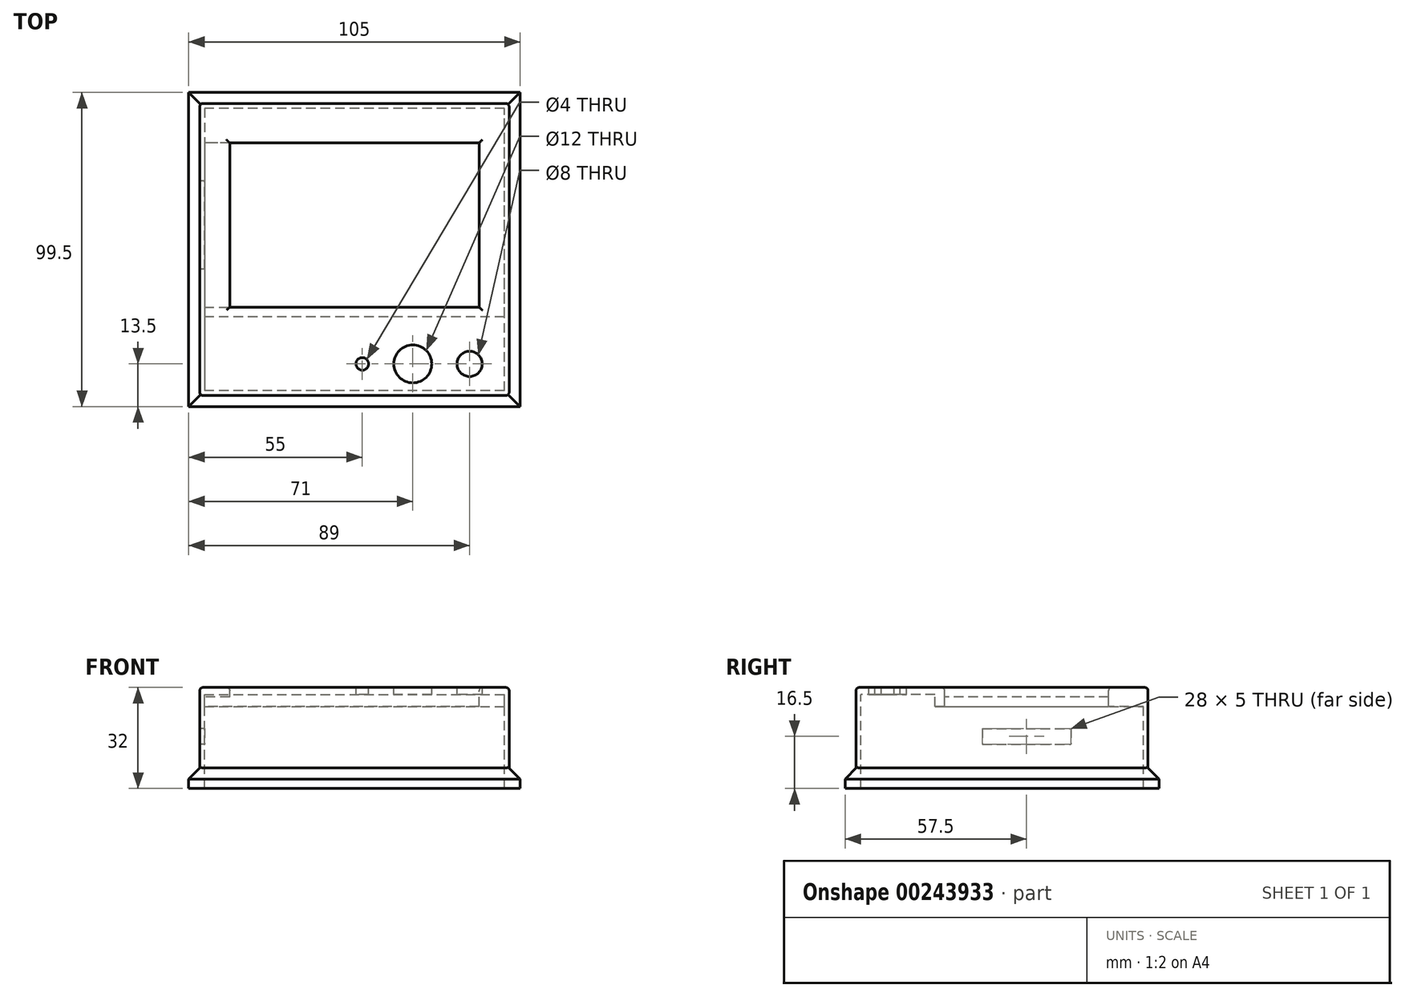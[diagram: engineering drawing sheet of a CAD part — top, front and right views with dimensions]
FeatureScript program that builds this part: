
annotation { "Feature Type Name" : "Feature", "Feature Type Description" : "" }
export const myFeature = defineFeature(function(context is Context, id is Id, definition is map)
    precondition{}
    {
        {
            var Q0;
            Q0=qCreatedBy(makeId("Top.planeOp"),FACE);
            var sketch = newSketch(context, id + "F0", { "sketchPlane" : qUnion([Q0])});
            skLineSegment(sketch, "E0", {"start": v(0, 0) * mm, "end": v(0, 52) * mm});
            skLineSegment(sketch, "E1", {"start": v(0, 52) * mm, "end": v(-87, 52) * mm});
            skLineSegment(sketch, "E2", {"start": v(-87, 0) * mm, "end": v(0, 0) * mm});
            skLineSegment(sketch, "E3.0", {"start": v(-87, 63) * mm, "end": v(-87, -26.5) * mm});
            skLineSegment(sketch, "E4.0", {"start": v(8, -26.5) * mm, "end": v(8, 63) * mm});
            skLineSegment(sketch, "E5.0", {"start": v(8, 63) * mm, "end": v(-87, 63) * mm});
            skLineSegment(sketch, "E6.0", {"start": v(-3, -5) * mm, "end": v(-3, -25) * mm, "construction": true});
            skLineSegment(sketch, "E7.0", {"start": v(-77, -18) * mm, "end": v(-3, -18) * mm, "construction": true});
            skLineSegment(sketch, "E8.0", {"start": v(-21, -5) * mm, "end": v(-21, -18) * mm, "construction": true});
            skLineSegment(sketch, "E9.0", {"start": v(-37, -5) * mm, "end": v(-37, -18) * mm, "construction": true});
            skCircle(sketch, "E10", {"center": v(-3, -18) * mm, "radius": 4 * mm});
            skCircle(sketch, "E11", {"center": v(-21, -18) * mm, "radius": 6 * mm});
            skCircle(sketch, "E12", {"center": v(-37, -18) * mm, "radius": 2 * mm});
            skPoint(sketch, "E13.orphan", {"position": v(-79, 0) * mm});
            skLineSegment(sketch, "E14.0", {"start": v(-88.5, 64.5) * mm, "end": v(-88.5, -28) * mm});
            skLineSegment(sketch, "E15.0", {"start": v(8, -26.5) * mm, "end": v(-87, -26.5) * mm});
            skLineSegment(sketch, "E16.0", {"start": v(9.5, -28) * mm, "end": v(9.5, 64.5) * mm});
            skLineSegment(sketch, "E17.0", {"start": v(9.5, 64.5) * mm, "end": v(-88.5, 64.5) * mm});
            skLineSegment(sketch, "E18.0", {"start": v(-79, 52) * mm, "end": v(-79, 0) * mm});
            skLineSegment(sketch, "E19.0", {"start": v(-77, -5) * mm, "end": v(-77, -18) * mm, "construction": true});
            skLineSegment(sketch, "E20.0", {"start": v(-77, -14) * mm, "end": v(-3, -14) * mm, "construction": true});
            skLineSegment(sketch, "E21.0", {"start": v(-87, -3) * mm, "end": v(8, -3) * mm});
            skLineSegment(sketch, "E22.0", {"start": v(9.5, -28) * mm, "end": v(-88.5, -28) * mm});
            skSolve(sketch);
        }
        {
            var Q0;
            {var subQ8=sQuery(id+"F0.wireOp",EDGE,"E0");Q0=makeQuery(id+"F0.imprint","IMPRINT",FACE,{"disambiguationData":[TD([[makeQuery(id+"F0.imprint","IMPRINT",EDGE,{"derivedFrom":subQ8}),-1.0]])]});}
            extrude(context, id + "F1", {"entities" : qUnion([Q0]), "oppositeDirection" : true, "depth" : 6 * mm});
        }
        {
            var Q0;
            {var subQ0=sQuery(id+"F0.wireOp",EDGE,"8c7ae999-3cc3-40bf-82e7-a0a417ca3e16.0");Q0=makeQuery(id+"F0.imprint","IMPRINT",FACE,{"disambiguationData":[TD([[makeQuery(id+"F0.imprint","IMPRINT",EDGE,{"derivedFrom":subQ0}),-1.0]])]});}
            var Q1;
            {var subQ3=sQuery(id+"F0.wireOp",EDGE,"E18.0");Q1=makeQuery(id+"F0.imprint","IMPRINT",FACE,{"disambiguationData":[TD([[makeQuery(id+"F0.imprint","IMPRINT",EDGE,{"derivedFrom":subQ3}),-1.0]])]});}
            extrude(context, id + "F2", {"entities" : qUnion([Q0, Q1]), "operationType" : NewBodyOperationType.ADD, "oppositeDirection" : true, "depth" : 3 * mm});
        }
        {
            var Q0;
            {var subQ1=sQuery(id+"F0.wireOp",EDGE,"E5.0");Q0=makeQuery(id+"F0.imprint","IMPRINT",FACE,{"disambiguationData":[TD([[makeQuery(id+"F0.imprint","IMPRINT",EDGE,{"derivedFrom":subQ1}),-1.0]])]});}
            extrude(context, id + "F3", {"entities" : qUnion([Q0]), "operationType" : NewBodyOperationType.ADD, "oppositeDirection" : true, "depth" : 32 * mm, "offsetDistance" : 25 * mm});
        }
        {
            var Q0;
            Q0=qCreatedBy(makeId("Right.planeOp"),FACE);
            cPlane(context, id + "F4", {"entities" : qUnion([Q0]), "cplaneType" : CPlaneType.OFFSET, "offset" : 88.5 * mm, "oppositeDirection" : true, "width" : 150 * mm, "height" : 150 * mm});
        }
        {
            var Q0;
            Q0=qCreatedBy(id+"F4.planeOp",FACE);
            var sketch = newSketch(context, id + "F5", { "sketchPlane" : qUnion([Q0])});
            skLineSegment(sketch, "E23.0", {"start": v(12, -13) * mm, "end": v(40, -13) * mm});
            skLineSegment(sketch, "E24.0", {"start": v(12, -18) * mm, "end": v(40, -18) * mm});
            skLineSegment(sketch, "E25.0", {"start": v(12, -13) * mm, "end": v(12, -18) * mm});
            skLineSegment(sketch, "E26.0", {"start": v(40, -13) * mm, "end": v(40, -18) * mm});
            skSolve(sketch);
        }
        {
            var Q0;
            Q0=makeQuery(id+"F5.imprint","IMPRINT",FACE,{"disambiguationData":[TD([[makeQuery(id+"F5.imprint","IMPRINT",EDGE,{"derivedFrom":sQuery(id+"F5.wireOp",EDGE,"E23.0")}),-1.0]])]});
            extrude(context, id + "F6", {"entities" : qUnion([Q0]), "operationType" : NewBodyOperationType.REMOVE, "depth" : 20 * mm});
        }
        {
            var Q0;
            Q0=makeQuery(id+"F0.imprint","IMPRINT",FACE,{"disambiguationData":[TD([[makeQuery(id+"F0.imprint","IMPRINT",EDGE,{"derivedFrom":sQuery(id+"F0.wireOp",EDGE,"E10")}),-1.0]])]});
            extrude(context, id + "F7", {"entities" : qUnion([Q0]), "operationType" : NewBodyOperationType.ADD, "oppositeDirection" : true, "depth" : 2.25 * mm});
        }
        {
            var Q0;
            Q0=qCreatedBy(makeId("Top.planeOp"),FACE);
            cPlane(context, id + "F8", {"entities" : qUnion([Q0]), "cplaneType" : CPlaneType.OFFSET, "offset" : 32 * mm, "oppositeDirection" : true, "width" : 150 * mm, "height" : 150 * mm});
        }
        {
            var Q0;
            Q0=qCreatedBy(id+"F8.planeOp",FACE);
            var sketch = newSketch(context, id + "F9", { "sketchPlane" : qUnion([Q0])});
            skLineSegment(sketch, "E27", {"start": v(0, 0) * mm, "end": v(8, 0) * mm, "construction": true});
            skLineSegment(sketch, "E28", {"start": v(8, 0) * mm, "end": v(8, -26.5) * mm, "construction": true});
            skLineSegment(sketch, "E29", {"start": v(8, -26.5) * mm, "end": v(-87, -26.5) * mm});
            skLineSegment(sketch, "E30", {"start": v(-87, -26.5) * mm, "end": v(-87, 63) * mm});
            skLineSegment(sketch, "E31", {"start": v(-87, 63) * mm, "end": v(8, 63) * mm});
            skLineSegment(sketch, "E32", {"start": v(8, 63) * mm, "end": v(8, -26.5) * mm});
            skLineSegment(sketch, "E33.0", {"start": v(13, 68) * mm, "end": v(13, -31.5) * mm});
            skLineSegment(sketch, "E34.0", {"start": v(13, -31.5) * mm, "end": v(-92, -31.5) * mm});
            skLineSegment(sketch, "E35.0", {"start": v(-92, -31.5) * mm, "end": v(-92, 68) * mm});
            skLineSegment(sketch, "E36.0", {"start": v(-92, 68) * mm, "end": v(13, 68) * mm});
            skSolve(sketch);
        }
        {
            var Q0;
            Q0=makeQuery(id+"F9.imprint","IMPRINT",FACE,{"disambiguationData":[TD([[makeQuery(id+"F9.imprint","IMPRINT",EDGE,{"derivedFrom":sQuery(id+"F9.wireOp",EDGE,"E29")}),1.0]])]});
            extrude(context, id + "F10", {"entities" : qUnion([Q0]), "operationType" : NewBodyOperationType.ADD, "depth" : 3 * mm, "offsetDistance" : 25 * mm});
        }
        {
            var Q0;
            Q0=makeQuery(id+"F10.boolean.opBoolean","INTERSECT",EDGE,{"derivedFrom":[makeQuery(id+"F3.opExtrude","SWEPT_FACE",FACE,{"disambiguationData":[OSD([sQuery(id+"F0.wireOp",EDGE,"E14.0")])]}),makeQuery(id+"F10.opExtrude","CAP_FACE",FACE,{"disambiguationData":[OSD([sQuery(id+"F9.wireOp",EDGE,"E29"),sQuery(id+"F9.wireOp",EDGE,"E30"),sQuery(id+"F9.wireOp",EDGE,"E31"),sQuery(id+"F9.wireOp",EDGE,"E32"),sQuery(id+"F9.wireOp",EDGE,"E33.0"),sQuery(id+"F9.wireOp",EDGE,"E34.0"),sQuery(id+"F9.wireOp",EDGE,"E35.0"),sQuery(id+"F9.wireOp",EDGE,"E36.0")])],"isStart":false})]});
            var Q1;
            Q1=makeQuery(id+"F10.boolean.opBoolean","INTERSECT",EDGE,{"derivedFrom":[makeQuery(id+"F3.opExtrude","SWEPT_FACE",FACE,{"disambiguationData":[OSD([sQuery(id+"F0.wireOp",EDGE,"E22.0")])]}),makeQuery(id+"F10.opExtrude","CAP_FACE",FACE,{"disambiguationData":[OSD([sQuery(id+"F9.wireOp",EDGE,"E29"),sQuery(id+"F9.wireOp",EDGE,"E30"),sQuery(id+"F9.wireOp",EDGE,"E31"),sQuery(id+"F9.wireOp",EDGE,"E32"),sQuery(id+"F9.wireOp",EDGE,"E33.0"),sQuery(id+"F9.wireOp",EDGE,"E34.0"),sQuery(id+"F9.wireOp",EDGE,"E35.0"),sQuery(id+"F9.wireOp",EDGE,"E36.0")])],"isStart":false})]});
            var Q2;
            Q2=makeQuery(id+"F10.boolean.opBoolean","INTERSECT",EDGE,{"derivedFrom":[makeQuery(id+"F3.opExtrude","SWEPT_FACE",FACE,{"disambiguationData":[OSD([sQuery(id+"F0.wireOp",EDGE,"E16.0")])]}),makeQuery(id+"F10.opExtrude","CAP_FACE",FACE,{"disambiguationData":[OSD([sQuery(id+"F9.wireOp",EDGE,"E29"),sQuery(id+"F9.wireOp",EDGE,"E30"),sQuery(id+"F9.wireOp",EDGE,"E31"),sQuery(id+"F9.wireOp",EDGE,"E32"),sQuery(id+"F9.wireOp",EDGE,"E33.0"),sQuery(id+"F9.wireOp",EDGE,"E34.0"),sQuery(id+"F9.wireOp",EDGE,"E35.0"),sQuery(id+"F9.wireOp",EDGE,"E36.0")])],"isStart":false})]});
            var Q3;
            Q3=makeQuery(id+"F10.boolean.opBoolean","INTERSECT",EDGE,{"derivedFrom":[makeQuery(id+"F3.opExtrude","SWEPT_FACE",FACE,{"disambiguationData":[OSD([sQuery(id+"F0.wireOp",EDGE,"E17.0")])]}),makeQuery(id+"F10.opExtrude","CAP_FACE",FACE,{"disambiguationData":[OSD([sQuery(id+"F9.wireOp",EDGE,"E29"),sQuery(id+"F9.wireOp",EDGE,"E30"),sQuery(id+"F9.wireOp",EDGE,"E31"),sQuery(id+"F9.wireOp",EDGE,"E32"),sQuery(id+"F9.wireOp",EDGE,"E33.0"),sQuery(id+"F9.wireOp",EDGE,"E34.0"),sQuery(id+"F9.wireOp",EDGE,"E35.0"),sQuery(id+"F9.wireOp",EDGE,"E36.0")])],"isStart":false})]});
            chamfer(context, id + "F11", {"entities" : qUnion([Q0, Q1, Q2, Q3]), "width" : 3.5 * mm, "tangentPropagation" : true});
        }
        {
            var Q0;
            Q0=makeQuery(id+"F3.opExtrude","SWEPT_EDGE",EDGE,{"disambiguationData":[OSD([sQuery(id+"F0.wireOp",EDGE,"E14.0"),sQuery(id+"F0.wireOp",EDGE,"E22.0")])]});
            var Q1;
            Q1=makeQuery(id+"F3.opExtrude","CAP_EDGE",EDGE,{"disambiguationData":[OSD([sQuery(id+"F0.wireOp",EDGE,"E22.0")])],"isStart":true});
            var Q2;
            Q2=makeQuery(id+"F3.opExtrude","CAP_EDGE",EDGE,{"disambiguationData":[OSD([sQuery(id+"F0.wireOp",EDGE,"E14.0")])],"isStart":true});
            var Q3;
            Q3=makeQuery(id+"F3.opExtrude","CAP_EDGE",EDGE,{"disambiguationData":[OSD([sQuery(id+"F0.wireOp",EDGE,"E17.0")])],"isStart":true});
            var Q4;
            Q4=makeQuery(id+"F3.opExtrude","CAP_EDGE",EDGE,{"disambiguationData":[OSD([sQuery(id+"F0.wireOp",EDGE,"E16.0")])],"isStart":true});
            var Q5;
            Q5=makeQuery(id+"F1.opExtrude","CAP_EDGE",EDGE,{"disambiguationData":[OSD([sQuery(id+"F0.wireOp",EDGE,"E0")])],"isStart":true});
            var Q6;
            Q6=makeQuery(id+"F1.opExtrude","CAP_EDGE",EDGE,{"disambiguationData":[OSD([sQuery(id+"F0.wireOp",EDGE,"E2")])],"isStart":true});
            var Q7;
            Q7=makeQuery(id+"F2.opExtrude","CAP_EDGE",EDGE,{"disambiguationData":[OSD([sQuery(id+"F0.wireOp",EDGE,"E18.0")])],"isStart":true});
            var Q8;
            Q8=makeQuery(id+"F1.opExtrude","CAP_EDGE",EDGE,{"disambiguationData":[OSD([sQuery(id+"F0.wireOp",EDGE,"E1")])],"isStart":true});
            var Q9;
            Q9=makeQuery(id+"F3.opExtrude","SWEPT_EDGE",EDGE,{"disambiguationData":[OSD([sQuery(id+"F0.wireOp",EDGE,"E16.0"),sQuery(id+"F0.wireOp",EDGE,"E22.0")])]});
            var Q10;
            Q10=makeQuery(id+"F3.opExtrude","SWEPT_EDGE",EDGE,{"disambiguationData":[OSD([sQuery(id+"F0.wireOp",EDGE,"E16.0"),sQuery(id+"F0.wireOp",EDGE,"E17.0")])]});
            var Q11;
            Q11=makeQuery(id+"F3.opExtrude","SWEPT_EDGE",EDGE,{"disambiguationData":[OSD([sQuery(id+"F0.wireOp",EDGE,"E14.0"),sQuery(id+"F0.wireOp",EDGE,"E17.0")])]});
            fillet(context, id + "F12", {"entities" : qUnion([Q0, Q1, Q2, Q3, Q4, Q5, Q6, Q7, Q8, Q9, Q10, Q11]), "radius" : 1 * mm, "tangentPropagation" : true, "allowEdgeOverflow" : false});
        }
    });
